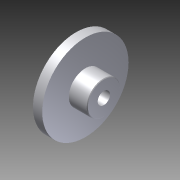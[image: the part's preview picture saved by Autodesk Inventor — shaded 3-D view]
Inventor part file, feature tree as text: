
AUTODESK INVENTOR PART (.ipt)
format: ipt  version: 2012 (Build 160160000, 160)  size: 598,528 bytes
history: native  units: in
note: dims shown in document units (in); Inventor stores cm internally (conversion verified against a paired STEP export)
features: extrude x2, sketch x1, imported_body x1
ambient origin geometry x8: Origin, YZ Plane, XZ Plane, XY Plane, X Axis, Y Axis, Z Axis, Center Point
feature tree (4):
  sketch  "Sketch1"  dims[d0=0.25in d1=0.5625in d2=0.0in d3=1.75in d4=1.0in d5=0.0in]
  extrude  "Extrusion1"  Depth=0.5625in TaperAngle=0.0deg
  extrude  "Extrusion2"  Depth=1.75in
  imported_body  "Base1"
